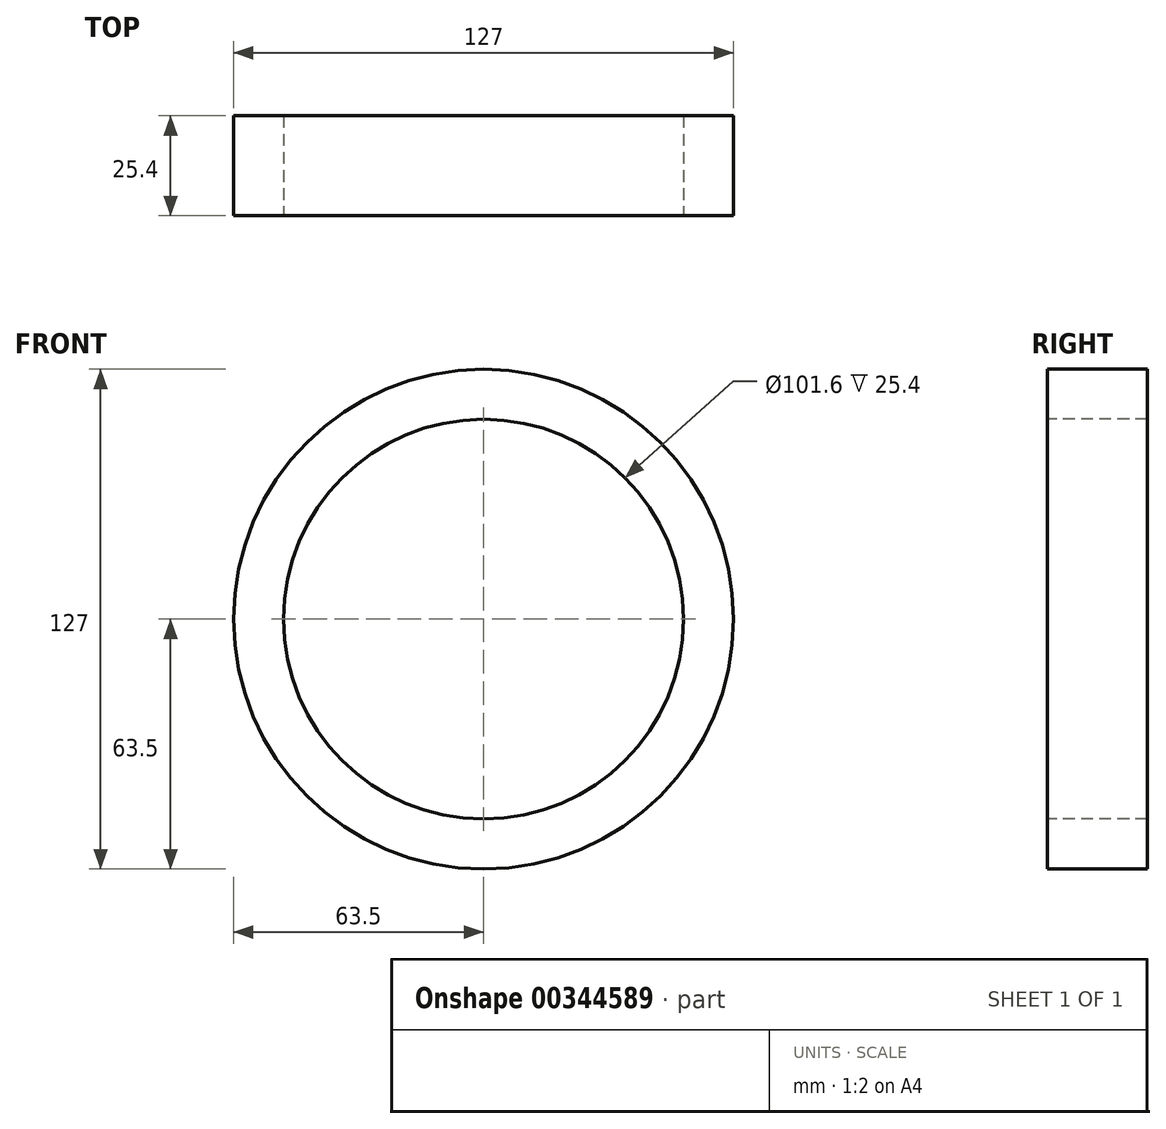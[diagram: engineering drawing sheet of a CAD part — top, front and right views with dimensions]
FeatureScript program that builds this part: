
annotation { "Feature Type Name" : "Feature", "Feature Type Description" : "" }
export const myFeature = defineFeature(function(context is Context, id is Id, definition is map)
    precondition{}
    {
        {
            var Q0;
            Q0=qCreatedBy(makeId("Front.planeOp"),FACE);
            var sketch = newSketch(context, id + "F0", { "sketchPlane" : qUnion([Q0])});
            skCircle(sketch, "E0", {"center": v(0, 0) * mm, "radius": 63.5 * mm});
            skSolve(sketch);
        }
        {
            var Q0;
            Q0=qCreatedBy(makeId("Front.planeOp"),FACE);
            cPlane(context, id + "F1", {"entities" : qUnion([Q0]), "cplaneType" : CPlaneType.OFFSET, "offset" : 25.4 * mm, "width" : 152.4 * mm, "height" : 152.4 * mm});
        }
        {
            var Q0;
            Q0=qCreatedBy(id+"F1.planeOp",FACE);
            var sketch = newSketch(context, id + "F2", { "sketchPlane" : qUnion([Q0])});
            skCircle(sketch, "E1", {"center": v(0, 0) * mm, "radius": 63.5 * mm});
            skSolve(sketch);
        }
        {
            var Q0;
            Q0=makeQuery(id+"F0.imprint","IMPRINT",FACE,{"disambiguationData":[TD([[makeQuery(id+"F0.imprint","IMPRINT",EDGE,{"derivedFrom":sQuery(id+"F0.wireOp",EDGE,"E0")}),1.0]])]});
            var Q1;
            Q1=makeQuery(id+"F2.imprint","IMPRINT",FACE,{"disambiguationData":[TD([[makeQuery(id+"F2.imprint","IMPRINT",EDGE,{"derivedFrom":sQuery(id+"F2.wireOp",EDGE,"E1")}),1.0]])]});
            loft(context, id + "F3", {"sheetProfilesArray" : [{ "sheetProfileEntities" : qUnion([Q0]) }, { "sheetProfileEntities" : qUnion([Q1]) }]});
        }
        {
            var Q0;
            Q0=makeQuery(id+"F3.opLoft","CAP_FACE",FACE,{"disambiguationData":[OSD([makeQuery(id+"F2.imprint","IMPRINT",FACE,{"disambiguationData":[TD([[makeQuery(id+"F2.imprint","IMPRINT",EDGE,{"derivedFrom":sQuery(id+"F2.wireOp",EDGE,"E1")}),1.0]])]})])],"isStart":true});
            var Q1;
            Q1=makeQuery(id+"F3.opLoft","CAP_FACE",FACE,{"disambiguationData":[OSD([makeQuery(id+"F0.imprint","IMPRINT",FACE,{"disambiguationData":[TD([[makeQuery(id+"F0.imprint","IMPRINT",EDGE,{"derivedFrom":sQuery(id+"F0.wireOp",EDGE,"E0")}),1.0]])]})])],"isStart":true});
            shell(context, id + "F4", {"entities" : qUnion([Q0, Q1]), "thickness" : 12.7 * mm});
        }
    });
